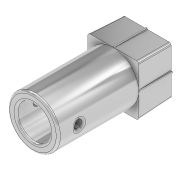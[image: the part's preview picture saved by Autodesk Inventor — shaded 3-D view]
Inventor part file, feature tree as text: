
AUTODESK INVENTOR PART (.ipt)
format: ipt  version: 2020 (Build 240168000, 168)  size: 292,864 bytes
history: native  units: in
note: dims shown in document units (in); Inventor stores cm internally (conversion verified against a paired STEP export)
features: extrude x6, fillet x6, sketch x5, projected_geometry x5, chamfer x4
ambient origin geometry x8: Origin, YZ Plane, XZ Plane, XY Plane, X Axis, Y Axis, Z Axis, Center Point
bodies: Solid1 (feature_tree)
feature tree (26):
  extrude  "Extrusion1"  Depth=0.315in
  extrude  "Extrusion2"  Depth=0.315in TaperAngle=0.0deg
  chamfer  "Chamfer1"  Distance=0.315in
  extrude  "Extrusion3"  Depth=0.0197in TaperAngle=0.0deg
  extrude  "Extrusion4"  Depth=0.3937in TaperAngle=0.0deg
  extrude  "Extrusion5"  Depth=0.0197in TaperAngle=0.0deg
  chamfer  "Chamfer2"  Distance=0.315in
  chamfer  "Chamfer3"  Distance=0.1969in
  chamfer  "Chamfer4"  Distance=0.315in
  fillet  "Fillet1"  Radius=0.315in
  fillet  "Fillet2"  Radius=0.315in
  fillet  "Fillet3"  Radius=0.0197in
  fillet  "Fillet4"  Radius=0.0197in
  extrude  "Extrusion6"  Depth=0.0197in
  fillet  "Fillet5"  Radius=0.0197in
  fillet  "Fillet6"  Radius=0.0157in
  sketch  "Sketch1"  dims[d0=0.4724in d1=0.315in]
  sketch  "Sketch2"  dims[d2=0.3346in d3=0.0in d10=0.315in d11=0.0in d12=0.315in d13=0.125in d14=0.0137in]
  sketch  "Sketch3"  dims[d15=0.4724in d16=0.0197in d17=0.0in]
  sketch  "Sketch4"  dims[d18=0.4724in d19=0.3937in d20=0.0in]
  sketch  "Sketch6"  dims[d21=0.0787in d22=0.197in d23=0.0in d24=0.315in d25=0.1969in d26=0.315in d27=0.125in d28=0.0137in d29=0.315in d30=0.125in d31=0.0137in d32=0.315in d33=0.125in d34=0.0137in d35=0.0197in d36=0.0197in d37=0.0197in d38=0.0197in d39=0.0157in d40=1.5748in d42=360.0deg d44=0.315in d45=0.0in d46=0.0079in d47=0.0197in]
  projected_geometry  "Projected Loop2"
  projected_geometry  "Projected Loop3"
  projected_geometry  "Projected Loop4"
  projected_geometry  "Projected Loop5"
  projected_geometry  "Projected Loop6"
